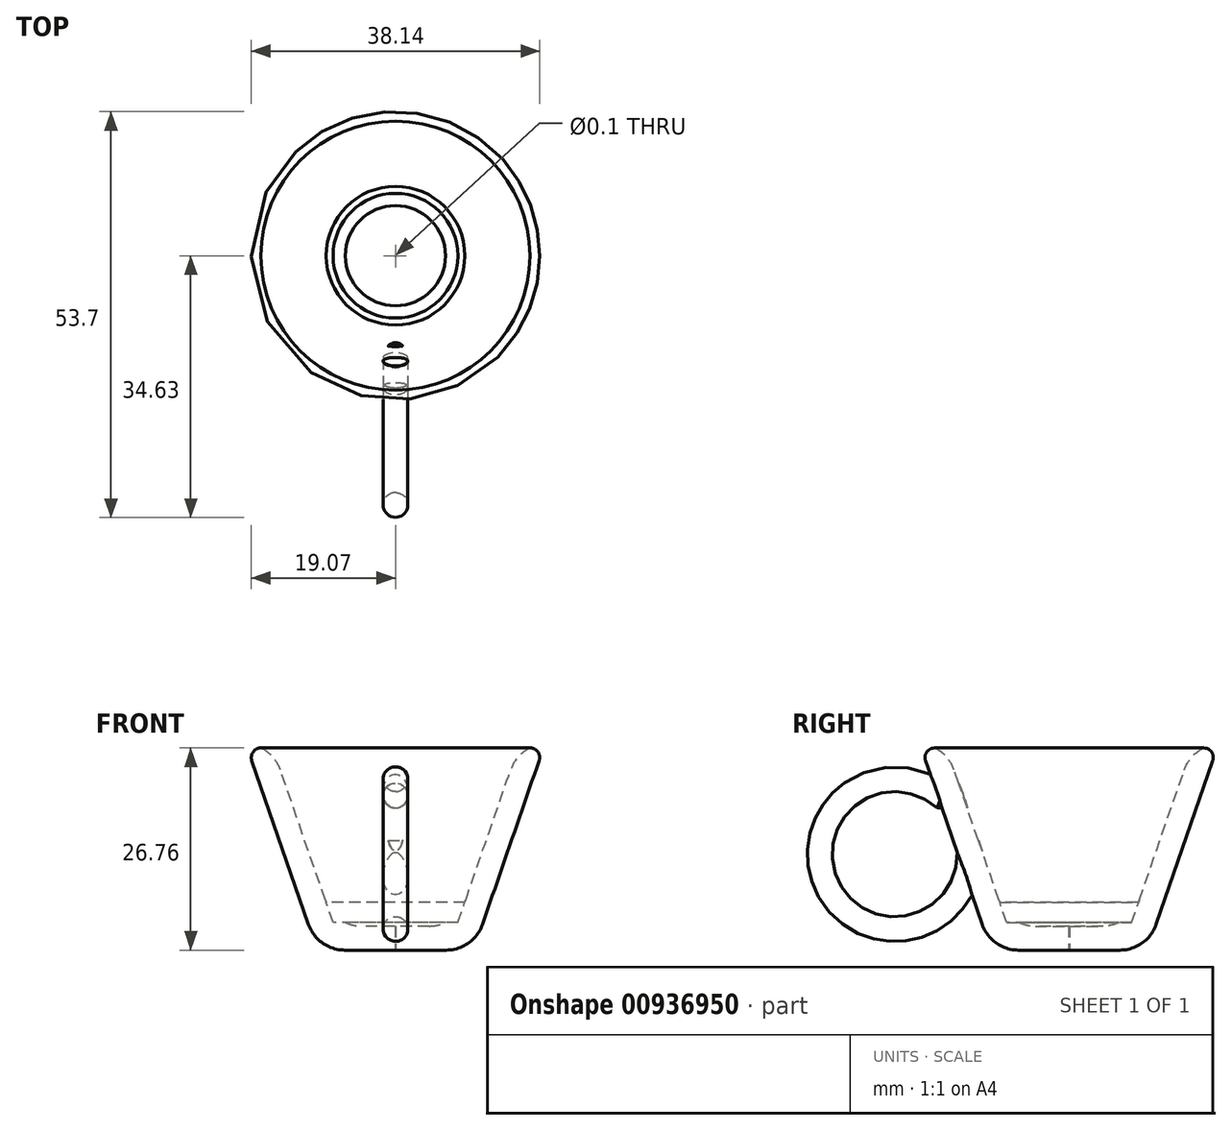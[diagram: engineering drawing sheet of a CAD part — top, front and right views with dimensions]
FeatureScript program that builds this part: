
annotation { "Feature Type Name" : "Feature", "Feature Type Description" : "" }
export const myFeature = defineFeature(function(context is Context, id is Id, definition is map)
    precondition{}
    {
        {
            var Q0;
            Q0=qCreatedBy(makeId("Front.planeOp"),FACE);
            var sketch = newSketch(context, id + "F0", { "sketchPlane" : qUnion([Q0])});
            skLineSegment(sketch, "E0", {"start": v(-19.58, 26.76) * mm, "end": v(-10.33, 0) * mm});
            skLineSegment(sketch, "E1.1", {"start": v(-16.24, 26.76) * mm, "end": v(-8.09, 3.18) * mm});
            skLineSegment(sketch, "E2", {"start": v(-19.58, 26.76) * mm, "end": v(-16.24, 26.76) * mm});
            skPoint(sketch, "E3.start.orphan", {"position": v(0, 3.1) * mm});
            skPoint(sketch, "E4.start.orphan", {"position": v(0, 0) * mm});
            skLineSegment(sketch, "E5", {"start": v(-8.09, 3.18) * mm, "end": v(-0.05, 3.18) * mm});
            skLineSegment(sketch, "E6", {"start": v(-0.05, 3.18) * mm, "end": v(-0.05, 0) * mm});
            skLineSegment(sketch, "E7", {"start": v(-0.05, 0) * mm, "end": v(-10.33, 0) * mm});
            skSolve(sketch);
        }
        {
            var Q0;
            Q0=qCreatedBy(makeId("Front.planeOp"),FACE);
            var sketch = newSketch(context, id + "F1", { "sketchPlane" : qUnion([Q0])});
            skLineSegment(sketch, "E8", {"start": v(0, 0) * mm, "end": v(0, 51.45) * mm});
            skSolve(sketch);
        }
        {
            var Q0;
            Q0=qCreatedBy(makeId("Front.planeOp"),FACE);
            var sketch = newSketch(context, id + "F2", { "sketchPlane" : qUnion([Q0])});
            skLineSegment(sketch, "E9", {"start": v(0, -16.69) * mm, "end": v(0, 39.08) * mm});
            skSolve(sketch);
        }
        {
            var Q0;
            Q0=makeQuery(id+"F0.imprint","IMPRINT",FACE,{"disambiguationData":[TD([[makeQuery(id+"F0.imprint","IMPRINT",EDGE,{"derivedFrom":sQuery(id+"F0.wireOp",EDGE,"E0")}),1.0]])]});
            var Q1;
            Q1=sQuery(id+"F2.wireOp",EDGE,"E9");
            revolve(context, id + "F3", {"surfaceOperationType" : NewSurfaceOperationType.NEW, "entities" : qUnion([Q0]), "axis" : qUnion([Q1]), "revolveType" : RevolveType.FULL});
        }
        {
            var Q0;
            Q0=makeQuery(id+"F3.opRevolve","SWEPT_EDGE",EDGE,{"disambiguationData":[OSD([sQuery(id+"F0.wireOp",EDGE,"E0"),sQuery(id+"F0.wireOp",EDGE,"E2")])]});
            fillet(context, id + "F4", {"entities" : qUnion([Q0]), "radius" : 1.27 * mm, "tangentPropagation" : true, "allowEdgeOverflow" : false});
        }
        {
            var Q0;
            Q0=makeQuery(id+"F3.opRevolve","SWEPT_EDGE",EDGE,{"disambiguationData":[OSD([sQuery(id+"F0.wireOp",EDGE,"E1.1"),sQuery(id+"F0.wireOp",EDGE,"E2")])]});
            fillet(context, id + "F5", {"entities" : qUnion([Q0]), "radius" : 5.08 * mm, "tangentPropagation" : true, "allowEdgeOverflow" : false});
        }
        {
            var Q0;
            Q0=makeQuery(id+"F3.opRevolve","SWEPT_EDGE",EDGE,{"disambiguationData":[OSD([sQuery(id+"F0.wireOp",EDGE,"E0"),sQuery(id+"F0.wireOp",EDGE,"E7")])]});
            fillet(context, id + "F6", {"entities" : qUnion([Q0]), "radius" : 5.08 * mm, "tangentPropagation" : true, "allowEdgeOverflow" : false});
        }
        {
            var Q0;
            Q0=makeQuery(id+"F3.opRevolve","SWEPT_EDGE",EDGE,{"disambiguationData":[OSD([sQuery(id+"F0.wireOp",EDGE,"E1.1"),sQuery(id+"F0.wireOp",EDGE,"E5")])]});
            fillet(context, id + "F7", {"entities" : qUnion([Q0]), "radius" : 5.08 * mm, "tangentPropagation" : true, "allowEdgeOverflow" : false});
        }
        {
            var Q0;
            Q0=qCreatedBy(makeId("Right.planeOp"),FACE);
            var sketch = newSketch(context, id + "F8", { "sketchPlane" : qUnion([Q0])});
            skArc(sketch, "E10", {"start": v(-13.71, 14.24) * mm, "mid": v(-31.3, 7.98) * mm, "end": v(-17.03, 20.02) * mm});
            skLineSegment(sketch, "E11", {"start": v(-17.03, 20.02) * mm, "end": v(0, 20.02) * mm});
            skSolve(sketch);
        }
        {
            var Q0;
            Q0=qCreatedBy(makeId("Front.planeOp"),FACE);
            var sketch = newSketch(context, id + "F9", { "sketchPlane" : qUnion([Q0])});
            skPoint(sketch, "E12.center.orphan", {"position": v(0, 20.45) * mm});
            skCircle(sketch, "E13", {"center": v(0, 20.45) * mm, "radius": 1.64 * mm});
            skSolve(sketch);
        }
        {
            var Q0;
            Q0 = qSketchRegion(id + "F9", true);
            var Q1;
            Q1=sQuery(id+"F8.wireOp",EDGE,"E11");
            var Q2;
            Q2=sQuery(id+"F8.wireOp",EDGE,"E10");
            sweep(context, id + "F10", {"operationType" : NewBodyOperationType.ADD, "profiles" : qUnion([Q0]), "path" : qUnion([Q1, Q2])});
        }
        {
            var Q0;
            Q0=qCreatedBy(makeId("Front.planeOp"),FACE);
            var sketch = newSketch(context, id + "F11", { "sketchPlane" : qUnion([Q0])});
            skLineSegment(sketch, "E14", {"start": v(0, 3.66) * mm, "end": v(-8.25, 3.66) * mm});
            skLineSegment(sketch, "E15", {"start": v(-8.25, 3.66) * mm, "end": v(-20.14, 38.15) * mm});
            skLineSegment(sketch, "E16", {"start": v(-20.14, 38.15) * mm, "end": v(0, 38.15) * mm});
            skLineSegment(sketch, "E17", {"start": v(0, 38.15) * mm, "end": v(0, 3.66) * mm});
            skSolve(sketch);
        }
        {
            var Q0;
            Q0=makeQuery(id+"F11.imprint","IMPRINT",FACE,{"disambiguationData":[TD([[makeQuery(id+"F11.imprint","IMPRINT",EDGE,{"derivedFrom":sQuery(id+"F11.wireOp",EDGE,"E14")}),-1.0]])]});
            var Q1;
            Q1=sQuery(id+"F1.wireOp",EDGE,"E8");
            revolve(context, id + "F12", {"operationType" : NewBodyOperationType.REMOVE, "surfaceOperationType" : NewSurfaceOperationType.NEW, "entities" : qUnion([Q0]), "axis" : qUnion([Q1]), "revolveType" : RevolveType.FULL, "oppositeDirection" : true});
        }
    });
